# Revit family: Toilet-Floor_Mount-KOHLER-San_Souci-K-4007
name_source: partatom
category: Plumbing Fixtures
revit_build: Autodesk Revit 2015 (Build: 20140606_1530(x64)
units: mm (PartAtom-declared; Revit-internal decimal feet)

## types (10) — shared parameters
ADA Compliant = No
Assembly Code = D2010100
CW Connection = Yes
Cold Water Inlet = Cold Water Inlet
Date Modified = 4/27/2018
Default Elevation = 0"
Description = One-piece round-front 1.28 gpf toilet with AquaPiston flushing technology
Flow Rate = 0 GPM
Flush Rate = 1.28 GPF
HW Connection = No
Height = 24 1/4"
Hot Water Inlet = Hot Water Inlet
Length = 25 5/8"
Manufacturer = KOHLER Co.
MasterFormat 1995 = 15410
MasterFormat 2004 = 22.41.13
Material = Vitreous china
Pressure = 80.00 psi
Product Documentation Link = http://www.us.kohler.com
Product Name = San Souci
Product Page URL = http://www.us.kohler.com
Rough-In = 12"
Seat Included = Yes
URL = https://www.us.kohler.com
Vent Connection = No
Waste Connection = Yes
Waste Water Outlet = Waste Water Outlet
Width = 16 3/4"

## per-type parameters (varying)
| type | Finish | Model | Type |
| 0-White | Kohler-Vitreous_China-0-White | K-4007-0 | 1 |
| 96-Biscuit | Kohler-Vitreous_China-96-Biscuit | K-4007-96 | 2 |
| 47-Almond | Kohler-Vitreous_China-47-Almond | K-4007-47 | 3 |
| NY-Dune | Kohler-Vitreous_China-NY-Dune | K-4007-NY | 4 |
| 95-Ice Grey | Kohler-Vitreous_China-95-Ice_Grey | K-4007-95 | 5 |
| G9-Sandbar | Kohler-Vitreous_China-G9-Sandbar | K-4007-G9 | 6 |
| 33-Mexican Sand | Kohler-Vitreous_China-33-Mexican_Sand | K-4007-33 | 7 |
| K4-Cashmere | Kohler-Vitreous_China-K4-Cashmere | K-4007-K4 | 8 |
| 58-Thunder Grey | Kohler-Vitreous_China-58-Thunder_Grey | K-4007-58 | 9 |
| 7-Black Black | Kohler-Vitreous_China-7-Black_Black | K-4007-7 | 10 |

## geometry (parser evidence)
native form markers: Blend x2, Sweep x3
no freeform markers — native parametric forms only
